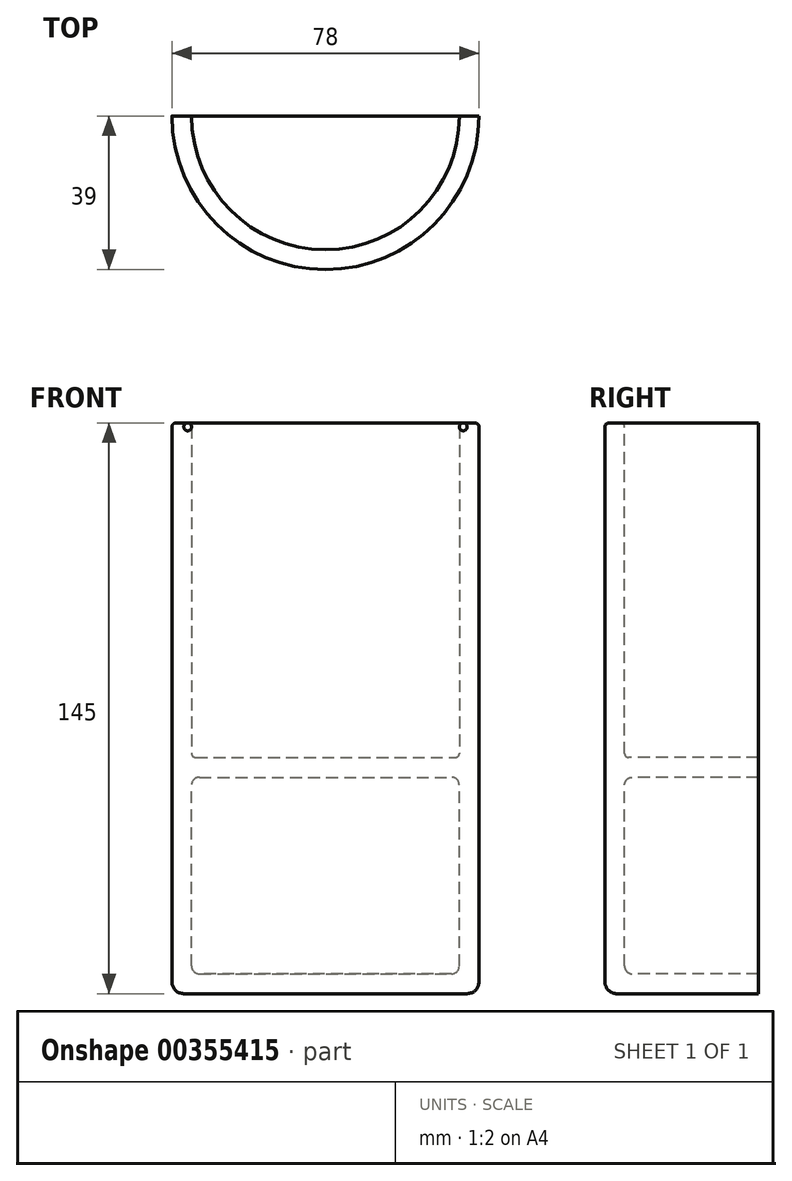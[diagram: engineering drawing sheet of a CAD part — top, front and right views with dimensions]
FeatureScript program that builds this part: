
annotation { "Feature Type Name" : "Feature", "Feature Type Description" : "" }
export const myFeature = defineFeature(function(context is Context, id is Id, definition is map)
    precondition{}
    {
        {
            var Q0;
            Q0=qCreatedBy(makeId("Front.planeOp"),FACE);
            var sketch = newSketch(context, id + "F0", { "sketchPlane" : qUnion([Q0])});
            skLineSegment(sketch, "E0", {"start": v(0, 161.65) * mm, "end": v(0, -240.28) * mm, "construction": true});
            skLineSegment(sketch, "E1", {"start": v(38, 43.81) * mm, "end": v(35, 43.81) * mm});
            skLineSegment(sketch, "E2", {"start": v(34, 42.81) * mm, "end": v(34, -40.19) * mm});
            skLineSegment(sketch, "E3", {"start": v(33, -41.19) * mm, "end": v(0, -41.19) * mm});
            skLineSegment(sketch, "E4", {"start": v(39, 42.81) * mm, "end": v(39, -98.19) * mm});
            skLineSegment(sketch, "E5", {"start": v(36, -101.19) * mm, "end": v(0, -101.19) * mm});
            skLineSegment(sketch, "E6", {"start": v(0, -101.19) * mm, "end": v(0, -96.19) * mm});
            skLineSegment(sketch, "E7", {"start": v(0, -96.19) * mm, "end": v(32, -96.19) * mm});
            skLineSegment(sketch, "E8", {"start": v(34, -94.19) * mm, "end": v(34, -48.19) * mm});
            skLineSegment(sketch, "E9", {"start": v(32, -46.19) * mm, "end": v(0, -46.19) * mm});
            skLineSegment(sketch, "E10", {"start": v(0, -46.19) * mm, "end": v(0, -41.19) * mm});
            skPoint(sketch, "E11.visualSharp", {"position": v(39, -101.19) * mm});
            skArc(sketch, "E11.filletArc", {"start": v(36, -101.19) * mm, "mid": v(38.12, -100.3) * mm, "end": v(39, -98.19) * mm});
            skPoint(sketch, "E12.visualSharp", {"position": v(39, 43.81) * mm});
            skArc(sketch, "E12.filletArc", {"start": v(39, 42.81) * mm, "mid": v(38.7, 43.52) * mm, "end": v(38, 43.81) * mm});
            skPoint(sketch, "E13.visualSharp", {"position": v(34, 43.81) * mm});
            skArc(sketch, "E13.filletArc", {"start": v(35, 43.81) * mm, "mid": v(34.3, 43.52) * mm, "end": v(34, 42.81) * mm});
            skPoint(sketch, "E14.visualSharp", {"position": v(34, -41.19) * mm});
            skArc(sketch, "E14.filletArc", {"start": v(33, -41.19) * mm, "mid": v(33.7, -40.9) * mm, "end": v(34, -40.19) * mm});
            skPoint(sketch, "E15.visualSharp", {"position": v(34, -96.19) * mm});
            skArc(sketch, "E15.filletArc", {"start": v(32, -96.19) * mm, "mid": v(33.41, -95.6) * mm, "end": v(34, -94.19) * mm});
            skPoint(sketch, "E16.visualSharp", {"position": v(34, -46.19) * mm});
            skArc(sketch, "E16.filletArc", {"start": v(34, -48.19) * mm, "mid": v(33.41, -46.77) * mm, "end": v(32, -46.19) * mm});
            skSolve(sketch);
        }
        {
            var Q0;
            Q0 = qSketchRegion(id + "F0", true);
            var Q1;
            Q1=sQuery(id+"F0.wireOp",EDGE,"E0");
            revolve(context, id + "F1", {"entities" : qUnion([Q0]), "axis" : qUnion([Q1]), "revolveType" : RevolveType.ONE_DIRECTION, "angle" : 180 * degree});
        }
    });
